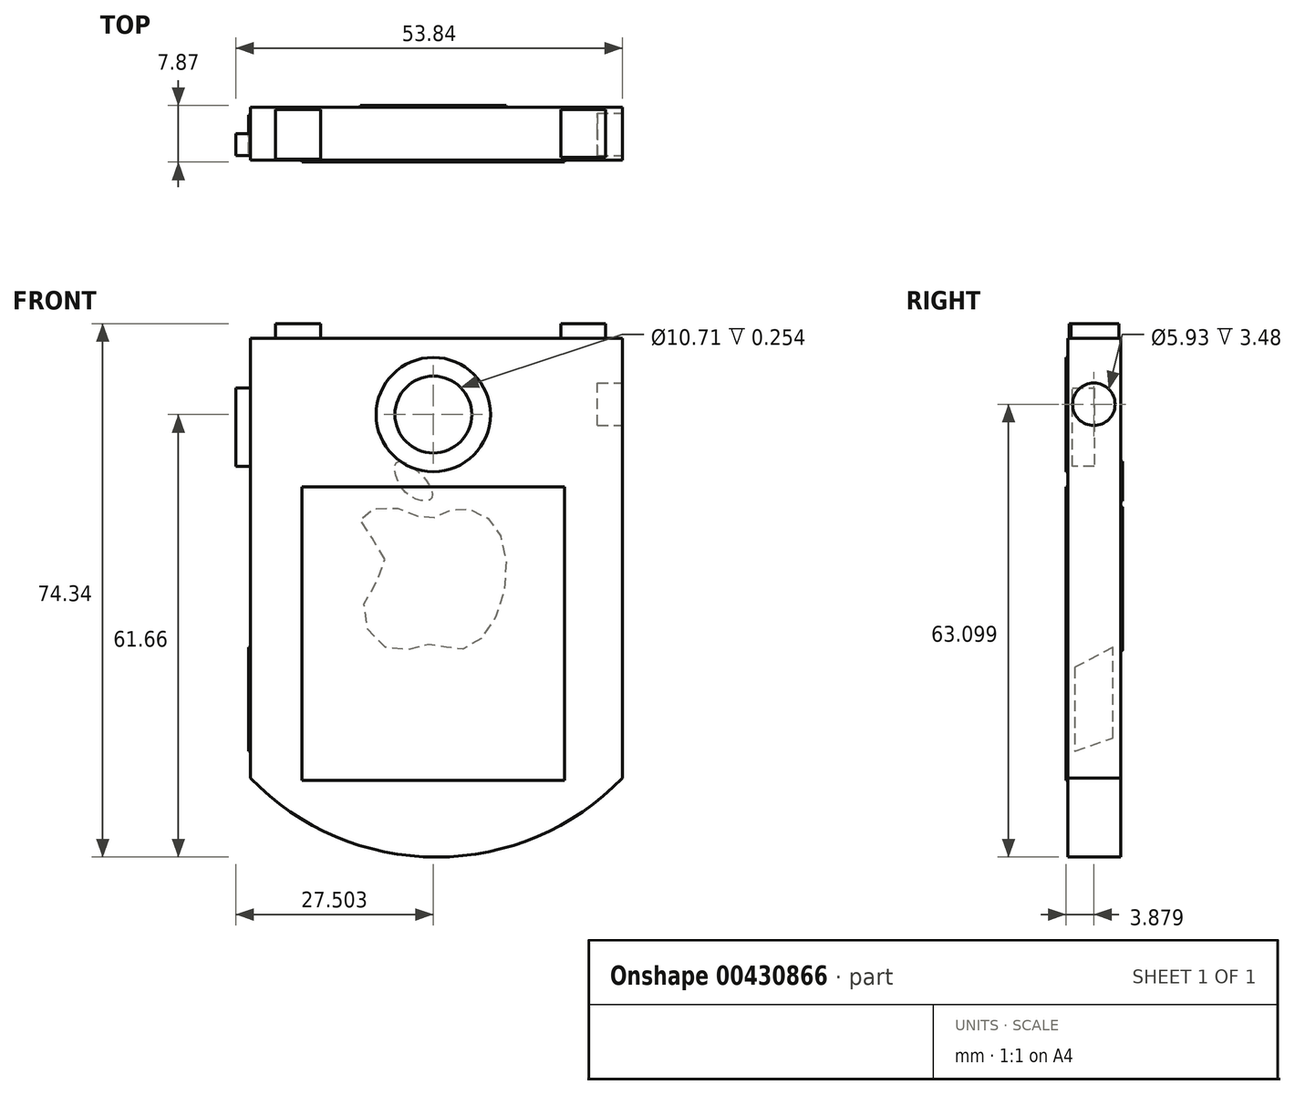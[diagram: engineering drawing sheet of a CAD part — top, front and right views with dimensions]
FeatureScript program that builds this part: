
annotation { "Feature Type Name" : "Feature", "Feature Type Description" : "" }
export const myFeature = defineFeature(function(context is Context, id is Id, definition is map)
    precondition{}
    {
        {
            var Q0;
            Q0=qCreatedBy(makeId("Front.planeOp"),FACE);
            var sketch = newSketch(context, id + "F0", { "sketchPlane" : qUnion([Q0])});
            skLineSegment(sketch, "E0", {"start": v(-56.7, 46.05) * mm, "end": v(-56.7, -15.25) * mm});
            skLineSegment(sketch, "E1", {"start": v(-4.9, 46.05) * mm, "end": v(-4.9, -15.25) * mm});
            skLineSegment(sketch, "E2", {"start": v(-56.7, 46.05) * mm, "end": v(-4.9, 46.05) * mm});
            skArc(sketch, "E3", {"start": v(-56.7, -15.25) * mm, "mid": v(-30.8, -26.26) * mm, "end": v(-4.9, -15.25) * mm});
            skSolve(sketch);
        }
        {
            var Q0;
            Q0 = qSketchRegion(id + "F0", true);
            extrude(context, id + "F1", {"entities" : qUnion([Q0]), "depth" : 7.37 * mm});
        }
        {
            var Q0;
            Q0=makeQuery(id+"F1.opExtrude","CAP_FACE",FACE,{"disambiguationData":[OSD([sQuery(id+"F0.wireOp",EDGE,"E0"),sQuery(id+"F0.wireOp",EDGE,"E1"),sQuery(id+"F0.wireOp",EDGE,"E2"),sQuery(id+"F0.wireOp",EDGE,"E3")])],"isStart":false});
            var sketch = newSketch(context, id + "F2", { "sketchPlane" : qUnion([Q0])});
            skLineSegment(sketch, "E4.bottom", {"start": v(-49.5, 25.33) * mm, "end": v(-12.95, 25.33) * mm});
            skLineSegment(sketch, "E4.top", {"start": v(-49.5, -15.54) * mm, "end": v(-12.95, -15.54) * mm});
            skLineSegment(sketch, "E4.left", {"start": v(-49.5, 25.33) * mm, "end": v(-49.5, -15.54) * mm});
            skLineSegment(sketch, "E4.right", {"start": v(-12.95, 25.33) * mm, "end": v(-12.95, -15.54) * mm});
            skCircle(sketch, "E5", {"center": v(-31.23, 35.4) * mm, "radius": 7.96 * mm});
            skPoint(sketch, "E5.centerSnap0", {"position": v(-31.23, 25.33) * mm});
            skCircle(sketch, "E6", {"center": v(-31.23, 35.4) * mm, "radius": 5.36 * mm});
            skSolve(sketch);
        }
        {
            var Q0;
            Q0 = qSketchRegion(id + "F2", true);
            extrude(context, id + "F3", {"entities" : qUnion([Q0]), "depth" : 0.25 * mm});
        }
        {
            var Q0;
            Q0=makeQuery(id+"F1.opExtrude","SWEPT_FACE",FACE,{"disambiguationData":[OSD([sQuery(id+"F0.wireOp",EDGE,"E0")])]});
            var sketch = newSketch(context, id + "F4", { "sketchPlane" : qUnion([Q0])});
            skLineSegment(sketch, "E7", {"start": v(3.68, 39.11) * mm, "end": v(3.68, 28.2) * mm});
            skPoint(sketch, "E7.startSnap0", {"position": v(3.68, 46.05) * mm});
            skLineSegment(sketch, "E8", {"start": v(3.68, 28.2) * mm, "end": v(6.71, 28.2) * mm});
            skLineSegment(sketch, "E9", {"start": v(6.71, 28.2) * mm, "end": v(6.71, 39.11) * mm});
            skLineSegment(sketch, "E10", {"start": v(6.71, 39.11) * mm, "end": v(3.68, 39.11) * mm});
            skLineSegment(sketch, "E11", {"start": v(3.68, 33.66) * mm, "end": v(6.71, 33.66) * mm});
            skSolve(sketch);
        }
        {
            var Q0;
            Q0 = qSketchRegion(id + "F4", true);
            extrude(context, id + "F5", {"entities" : qUnion([Q0]), "depth" : 2.03 * mm});
        }
        {
            var Q0;
            Q0=makeQuery(id+"F1.opExtrude","SWEPT_FACE",FACE,{"disambiguationData":[OSD([sQuery(id+"F0.wireOp",EDGE,"E0")])]});
            var sketch = newSketch(context, id + "F6", { "sketchPlane" : qUnion([Q0])});
            skLineSegment(sketch, "E12", {"start": v(1.06, 3) * mm, "end": v(6.39, 0.15) * mm});
            skLineSegment(sketch, "E13", {"start": v(6.39, 0.15) * mm, "end": v(6.39, -11.5) * mm});
            skLineSegment(sketch, "E14", {"start": v(6.39, -11.5) * mm, "end": v(1.06, -9.65) * mm});
            skLineSegment(sketch, "E15", {"start": v(1.06, -9.65) * mm, "end": v(1.06, 3) * mm});
            skSolve(sketch);
        }
        {
            var Q0;
            Q0=makeQuery(id+"F6.imprint","IMPRINT",FACE,{"disambiguationData":[TD([[makeQuery(id+"F6.imprint","IMPRINT",EDGE,{"derivedFrom":sQuery(id+"F6.wireOp",EDGE,"E12")}),-1.0]])]});
            extrude(context, id + "F7", {"entities" : qUnion([Q0]), "depth" : 0.25 * mm});
        }
        {
            var Q0;
            Q0=makeQuery(id+"F1.opExtrude","SWEPT_FACE",FACE,{"disambiguationData":[OSD([sQuery(id+"F0.wireOp",EDGE,"E2")])]});
            var sketch = newSketch(context, id + "F8", { "sketchPlane" : qUnion([Q0])});
            skLineSegment(sketch, "E16.bottom", {"start": v(-53.24, -0.29) * mm, "end": v(-46.91, -0.29) * mm});
            skLineSegment(sketch, "E16.top", {"start": v(-53.24, -7.2) * mm, "end": v(-46.91, -7.2) * mm});
            skLineSegment(sketch, "E16.left", {"start": v(-53.24, -0.29) * mm, "end": v(-53.24, -7.2) * mm});
            skLineSegment(sketch, "E16.right", {"start": v(-46.91, -0.29) * mm, "end": v(-46.91, -7.2) * mm});
            skLineSegment(sketch, "E17.bottom", {"start": v(-13.45, -0.27) * mm, "end": v(-7.24, -0.27) * mm});
            skLineSegment(sketch, "E17.top", {"start": v(-13.45, -6.94) * mm, "end": v(-7.24, -6.94) * mm});
            skLineSegment(sketch, "E17.left", {"start": v(-13.45, -0.27) * mm, "end": v(-13.45, -6.94) * mm});
            skLineSegment(sketch, "E17.right", {"start": v(-7.24, -0.27) * mm, "end": v(-7.24, -6.94) * mm});
            skSolve(sketch);
        }
        {
            var Q0;
            Q0 = qSketchRegion(id + "F8", true);
            extrude(context, id + "F9", {"entities" : qUnion([Q0]), "depth" : 2.03 * mm});
        }
        {
            var Q0;
            Q0=makeQuery(id+"F1.opExtrude","SWEPT_FACE",FACE,{"disambiguationData":[OSD([sQuery(id+"F0.wireOp",EDGE,"E1")])]});
            var sketch = newSketch(context, id + "F10", { "sketchPlane" : qUnion([Q0])});
            skCircle(sketch, "E18", {"center": v(-3.74, 36.84) * mm, "radius": 2.96 * mm});
            skSolve(sketch);
        }
        {
            var Q0;
            Q0 = qSketchRegion(id + "F10", true);
            extrude(context, id + "F11", {"entities" : qUnion([Q0]), "operationType" : NewBodyOperationType.REMOVE, "oppositeDirection" : true, "depth" : 3.48 * mm});
        }
        {
            var Q0;
            Q0=makeQuery(id+"F1.opExtrude","CAP_FACE",FACE,{"disambiguationData":[OSD([sQuery(id+"F0.wireOp",EDGE,"E0"),sQuery(id+"F0.wireOp",EDGE,"E1"),sQuery(id+"F0.wireOp",EDGE,"E2"),sQuery(id+"F0.wireOp",EDGE,"E3")])],"isStart":true});
            var sketch = newSketch(context, id + "F12", { "sketchPlane" : qUnion([Q0])});
            skFitSpline(sketch, "E19", {"points": [v(37.97, 15.25) * mm, v(41.4, 20.78) * mm, v(36.87, 22.48) * mm, v(32, 20.9) * mm, v(28.46, 22.2) * mm, v(23.89, 21.17) * mm, v(21.14, 15.53) * mm, v(23.18, 5.97) * mm, v(27.74, 2.62) * mm, v(31.29, 3.43) * mm, v(36.97, 2.61) * mm, v(41, 8.4) * mm, v(37.97, 15.25) * mm]});
            skFitSpline(sketch, "E20", {"points": [v(36.4, 28.7) * mm, v(33.21, 27.33) * mm, v(31.5, 23.71) * mm, v(35.02, 24.49) * mm, v(36.4, 28.7) * mm]});
            skSolve(sketch);
        }
        {
            var Q0;
            Q0 = qSketchRegion(id + "F12", true);
            extrude(context, id + "F13", {"entities" : qUnion([Q0]), "depth" : 0.25 * mm});
        }
    });
